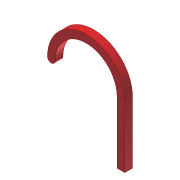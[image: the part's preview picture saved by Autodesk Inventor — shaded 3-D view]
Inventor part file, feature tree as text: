
AUTODESK INVENTOR PART (.ipt)
format: ipt  version: 2012 (Build 160160000, 160)  size: 79,872 bytes
history: native  units: in
note: dims shown in document units (in); Inventor stores cm internally (conversion verified against a paired STEP export)
features: extrude x1, sketch x1
ambient origin geometry x8: Origin, YZ Plane, XZ Plane, XY Plane, X Axis, Y Axis, Z Axis, Center Point
bodies: Solid1 (feature_tree)
feature tree (2):
  extrude  "Extrusion1"  Depth=1.0in
  sketch  "Sketch1"  dims[d0=0.25in d1=1.0in d2=2.0in d3=0.25in d4=0.0in]
